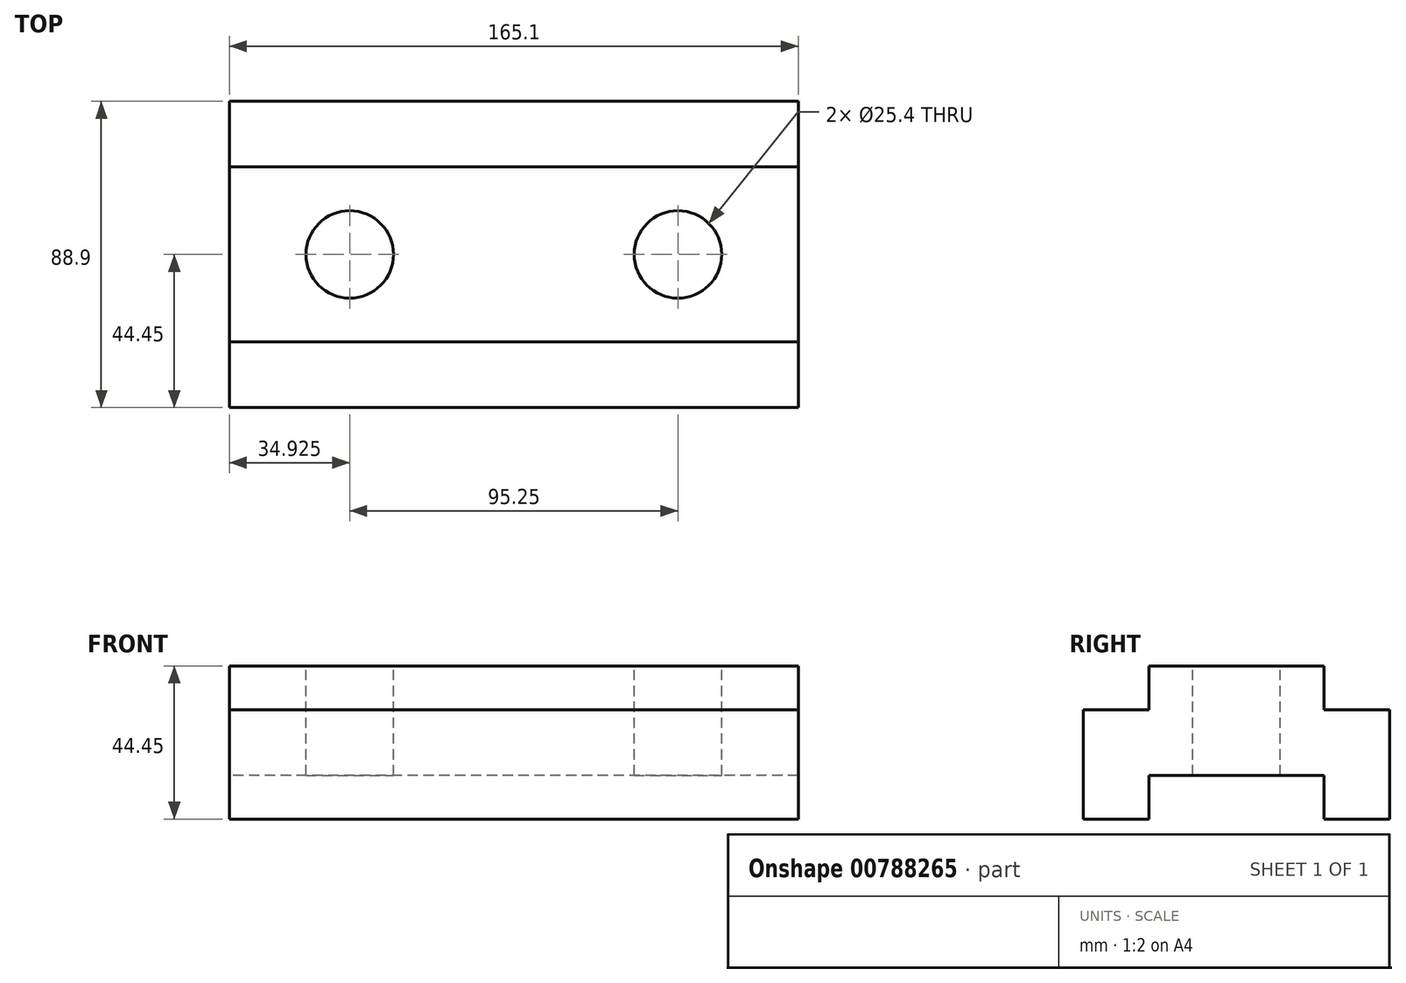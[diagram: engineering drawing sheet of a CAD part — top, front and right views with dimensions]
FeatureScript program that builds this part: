
annotation { "Feature Type Name" : "Feature", "Feature Type Description" : "" }
export const myFeature = defineFeature(function(context is Context, id is Id, definition is map)
    precondition{}
    {
        {
            var Q0;
            Q0=qCreatedBy(makeId("Right.planeOp"),FACE);
            var sketch = newSketch(context, id + "F0", { "sketchPlane" : qUnion([Q0])});
            skLineSegment(sketch, "E0", {"start": v(0, 0) * mm, "end": v(19.05, 0) * mm});
            skLineSegment(sketch, "E1", {"start": v(0, 0) * mm, "end": v(0, 31.75) * mm});
            skLineSegment(sketch, "E2", {"start": v(0, 31.75) * mm, "end": v(19.05, 31.75) * mm});
            skLineSegment(sketch, "E3", {"start": v(19.05, 31.75) * mm, "end": v(19.05, 44.45) * mm});
            skLineSegment(sketch, "E4", {"start": v(19.05, 44.45) * mm, "end": v(69.85, 44.45) * mm});
            skLineSegment(sketch, "E5", {"start": v(69.85, 44.45) * mm, "end": v(69.85, 31.75) * mm});
            skLineSegment(sketch, "E6", {"start": v(69.85, 31.75) * mm, "end": v(88.9, 31.75) * mm});
            skLineSegment(sketch, "E7", {"start": v(88.9, 31.75) * mm, "end": v(88.9, 0) * mm});
            skLineSegment(sketch, "E8", {"start": v(88.9, 0) * mm, "end": v(69.85, 0) * mm});
            skLineSegment(sketch, "E9", {"start": v(69.85, 0) * mm, "end": v(69.85, 12.7) * mm});
            skLineSegment(sketch, "E10", {"start": v(69.85, 12.7) * mm, "end": v(19.05, 12.7) * mm});
            skLineSegment(sketch, "E11", {"start": v(19.05, 12.7) * mm, "end": v(19.05, 0) * mm});
            skSolve(sketch);
        }
        {
            var Q0;
            Q0=makeQuery(id+"F0.imprint","IMPRINT",FACE,{"disambiguationData":[TD([[makeQuery(id+"F0.imprint","IMPRINT",EDGE,{"derivedFrom":sQuery(id+"F0.wireOp",EDGE,"E0")}),1.0]])]});
            extrude(context, id + "F1", {"entities" : qUnion([Q0]), "depth" : 165.1 * mm, "offsetDistance" : 25.4 * mm});
        }
        {
            var Q0;
            Q0=makeQuery(id+"F1.opExtrude","SWEPT_FACE",FACE,{"disambiguationData":[OSD([sQuery(id+"F0.wireOp",EDGE,"E4")])]});
            var sketch = newSketch(context, id + "F2", { "sketchPlane" : qUnion([Q0])});
            skLineSegment(sketch, "E12", {"start": v(0, 44.45) * mm, "end": v(34.92, 44.45) * mm, "construction": true});
            skLineSegment(sketch, "E13", {"start": v(34.92, 44.45) * mm, "end": v(130.18, 44.45) * mm, "construction": true});
            skCircle(sketch, "E14", {"center": v(34.92, 44.45) * mm, "radius": 12.7 * mm});
            skCircle(sketch, "E15", {"center": v(130.18, 44.45) * mm, "radius": 12.7 * mm});
            skSolve(sketch);
        }
        {
            var Q0;
            Q0 = qSketchRegion(id + "F2", true);
            extrude(context, id + "F3", {"entities" : qUnion([Q0]), "operationType" : NewBodyOperationType.REMOVE, "endBound" : BoundingType.UP_TO_NEXT, "oppositeDirection" : true, "depth" : 25.4 * mm, "offsetDistance" : 25.4 * mm});
        }
    });
